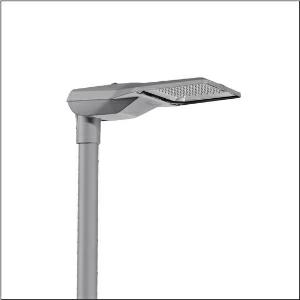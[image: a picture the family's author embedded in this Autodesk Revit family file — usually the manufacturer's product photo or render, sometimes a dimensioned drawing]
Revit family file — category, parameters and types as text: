
# Revit family: streetlight_sl_21_midi___st0_5a_5xe3b33s08lb_3b8c
name_source: partatom
category: Lighting Fixtures
units: mm (PartAtom-declared; Revit-internal decimal feet)

## family parameters
Cut with Voids When Loaded = No
Host = Face
Light Source = No
Part Type = Normal
Room Calculation Point = No
Round Connector Dimension = Use Diameter
Shared = No

## types (1)
- --- (1 x LED, 14340 lm, 98.3 W, 3000K)
    Apparent Load = 98 VA
    CIE Flux Codes = 41 75 97 100 100
    Color Rendering = 70
    Color Temperature = 3000K
    Default Elevation = 1800 mm
    Description = Streetlight SL 21 midi, mast luminaire, primary light control with lens, of PMMA, primary optical cover: cover, of toughened safety glass, transparent, light distribution: ST0.5a, light emission: direct distribution, primary light characteristic: asymmetric, installation type: side-entry, post-top, LED, High Power LED, rated luminous flux: 14.340lm, luminous efficacy: 146lm/W, light colour: 730, colour temperature: 3000K, control: overheat protection, constant luminous flux control, time-dependent luminous flux control, flexible luminous flux parameterisation, presetting dimming logarithmic, mains connection: 230..240V, AC, 50/60Hz, start of lifetime: 98W, end of service life: 101W, reduction: 45W, luminaire housing, of diecast aluminium, powder-coated, Siteco® metallic grey (DB 702S), corrosivity category C5 mid according to DIN EN ISO 12944, please order mast flange separately, inclination adjustable: 0°, 5°, 10°, 15°, sealing non-destructively replaceable, multi-level sealing system, length: 644mm, width: 335mm, height: 110mm, mast flange for spigot size: 42mm (side-entry): 5XC10008XM4, 60/48mm (side-entry/post-top): 5XC10108XM2, 76/60mm (side-entry/post-top): 5XC10108XM1, Smart Interface above, protection rating (complete): IP66, insulation class (complete): insulation class II (safety insulation), certification: CE, ENEC, ENEC+, VDE, impact resistance: IK09, permissible operating ambient temperature for outdoor applications: -40..+50°C, standard-compliant lighting for roads and squares, packaging unit: 1 piece

Light Distribution: ST0.5a
    Height = 111 mm
    Lamp = 1 x LED
    Lamp Light Flux = 14340 lm
    Lamp Power = 98.3 W
    Lamp count = 1
    Length = 644 mm
    Luminous efficacy = 146 lm/W
    Manufacturer = Siteco
    ModVariant = No
    Model = 5XE3B33S08LB
    Number of Poles = 1
    OnlyDefault = Yes
    Power Factor = 1
    Product Name = Streetlight SL 21 midi | ST0.5a
    Product group = mast luminaire | pylon top
    ProductGroupID = 6100
    Protection Class = Protection class II
    Protection Degree = IP 66
    RLX_Detail_Level = 1
    RLX_Emergency_Light_Flux = 0 lm
    RLX_Emergency_Type = 0
    RLX_Emergency_Type_DB = No
    RlxData = <blob elided: 101709 chars, md5=69fef3a1>
    Socket = socket
    Standby Power = 0 W
    System Light Flux = 14340 lm
    System Power = 98 W
    Type Comments = factory setting: luminous flux: 100 % | dim-lin: 254 | 1020 mA
    Type Image = l_1004302.jpg
    URL = http://relux.com
    VarID = @adj_144349
    Voltage = 0 V
    Weight = 0.00 kg
    Width = 336 mm

## geometry (parser evidence)
native form markers: Blend x4, Sweep x11
no freeform markers — native parametric forms only
